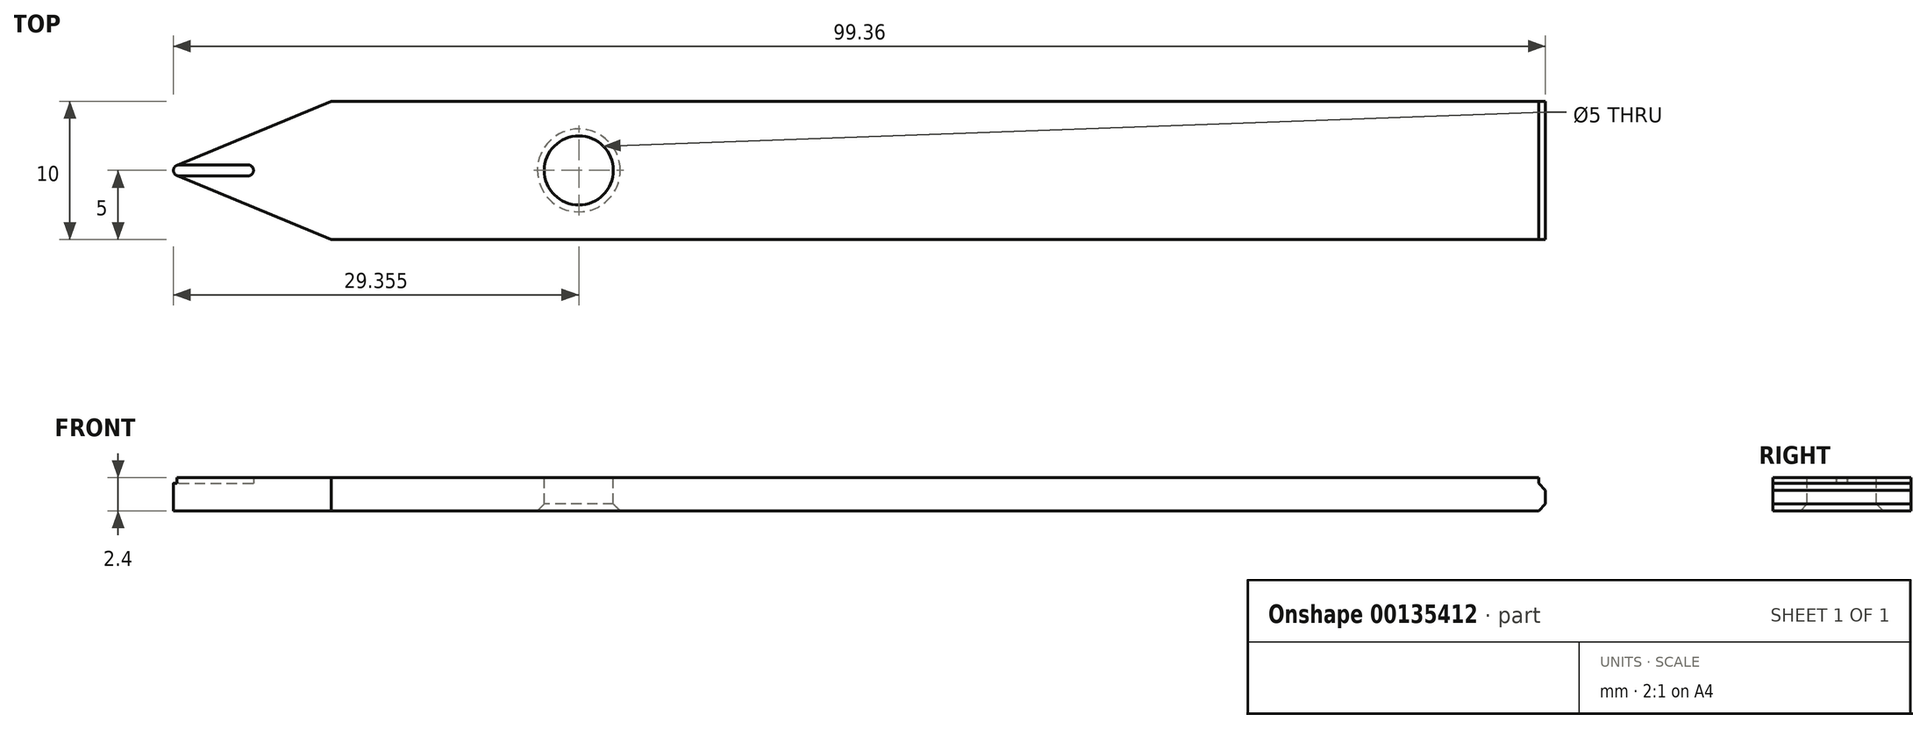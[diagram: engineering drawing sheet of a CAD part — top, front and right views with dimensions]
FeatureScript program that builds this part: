
annotation { "Feature Type Name" : "Feature", "Feature Type Description" : "" }
export const myFeature = defineFeature(function(context is Context, id is Id, definition is map)
    precondition{}
    {
        {
            var Q0;
            Q0=qCreatedBy(makeId("Top.planeOp"),FACE);
            var sketch = newSketch(context, id + "F0", { "sketchPlane" : qUnion([Q0])});
            skLineSegment(sketch, "E0", {"start": v(1.57, 0) * mm, "end": v(-86.36, 0) * mm});
            skLineSegment(sketch, "E1", {"start": v(-86.36, 0) * mm, "end": v(-98.43, -5) * mm});
            skLineSegment(sketch, "E2", {"start": v(-98.43, -5) * mm, "end": v(-86.36, -10) * mm});
            skLineSegment(sketch, "E3", {"start": v(-86.36, -10) * mm, "end": v(1.57, -10) * mm});
            skLineSegment(sketch, "E4", {"start": v(1.57, -10) * mm, "end": v(1.57, 0) * mm});
            skLineSegment(sketch, "E5", {"start": v(-98.43, -5) * mm, "end": v(-67.6, -5) * mm, "construction": true});
            skSolve(sketch);
        }
        {
            var Q0;
            Q0 = qSketchRegion(id + "F0", true);
            extrude(context, id + "F1", {"entities" : qUnion([Q0]), "depth" : 2 * mm});
        }
        {
            var Q0;
            Q0=makeQuery(id+"F1.opExtrude","CAP_FACE",FACE,{"disambiguationData":[OSD([sQuery(id+"F0.wireOp",EDGE,"E0"),sQuery(id+"F0.wireOp",EDGE,"E1"),sQuery(id+"F0.wireOp",EDGE,"E2"),sQuery(id+"F0.wireOp",EDGE,"E3"),sQuery(id+"F0.wireOp",EDGE,"E4")])],"isStart":false});
            var sketch = newSketch(context, id + "F2", { "sketchPlane" : qUnion([Q0])});
            skLineSegment(sketch, "E6", {"start": v(-98.43, -5) * mm, "end": v(-68.43, -5) * mm, "construction": true});
            skCircle(sketch, "E7", {"center": v(-68.43, -5) * mm, "radius": 2.5 * mm});
            skSolve(sketch);
        }
        {
            var Q0;
            Q0 = qSketchRegion(id + "F2", true);
            var Q1;
            Q1=makeQuery(id+"F2.imprint","IMPRINT",FACE,{"disambiguationData":[TD([[makeQuery(id+"F2.imprint","IMPRINT",EDGE,{"derivedFrom":sQuery(id+"F2.wireOp",EDGE,"E7")}),1.0]])]});
            extrude(context, id + "F3", {"entities" : qUnion([Q0, Q1]), "operationType" : NewBodyOperationType.REMOVE, "oppositeDirection" : true, "depth" : 25 * mm});
        }
        {
            var Q0;
            Q0=makeQuery(id+"F3.boolean.opBoolean","COPY",EDGE,{"derivedFrom":makeQuery(id+"F3.opExtrude","CAP_EDGE",EDGE,{"disambiguationData":[OSD([sQuery(id+"F2.wireOp",EDGE,"E7")])],"isStart":true})});
            var Q1;
            Q1=makeQuery(id+"F3.boolean.opBoolean","INTERSECT",EDGE,{"derivedFrom":[makeQuery(id+"F1.opExtrude","CAP_FACE",FACE,{"disambiguationData":[OSD([sQuery(id+"F0.wireOp",EDGE,"E0"),sQuery(id+"F0.wireOp",EDGE,"E1"),sQuery(id+"F0.wireOp",EDGE,"E2"),sQuery(id+"F0.wireOp",EDGE,"E3"),sQuery(id+"F0.wireOp",EDGE,"E4")])],"isStart":true}),makeQuery(id+"F3.opExtrude","SWEPT_FACE",FACE,{"disambiguationData":[OSD([sQuery(id+"F2.wireOp",EDGE,"E7")])]})]});
            chamfer(context, id + "F4", {"entities" : qUnion([Q0, Q1]), "width" : 0.5 * mm, "tangentPropagation" : true});
        }
        {
            var Q0;
            Q0=makeQuery(id+"F1.opExtrude","CAP_EDGE",EDGE,{"disambiguationData":[OSD([sQuery(id+"F0.wireOp",EDGE,"E4")])],"isStart":false});
            var Q1;
            Q1=makeQuery(id+"F1.opExtrude","CAP_EDGE",EDGE,{"disambiguationData":[OSD([sQuery(id+"F0.wireOp",EDGE,"E4")])],"isStart":true});
            chamfer(context, id + "F5", {"entities" : qUnion([Q0, Q1]), "width" : 0.5 * mm, "tangentPropagation" : true});
        }
        {
            var Q0;
            Q0=makeQuery(id+"F1.opExtrude","SWEPT_EDGE",EDGE,{"disambiguationData":[OSD([sQuery(id+"F0.wireOp",EDGE,"E1"),sQuery(id+"F0.wireOp",EDGE,"E2")])]});
            fillet(context, id + "F6", {"entities" : qUnion([Q0]), "radius" : 0.4 * mm, "tangentPropagation" : true, "allowEdgeOverflow" : false});
        }
        {
            var Q0;
            Q0=makeQuery(id+"F1.opExtrude","CAP_FACE",FACE,{"disambiguationData":[OSD([sQuery(id+"F0.wireOp",EDGE,"E0"),sQuery(id+"F0.wireOp",EDGE,"E1"),sQuery(id+"F0.wireOp",EDGE,"E2"),sQuery(id+"F0.wireOp",EDGE,"E3"),sQuery(id+"F0.wireOp",EDGE,"E4")])],"isStart":false});
            var sketch = newSketch(context, id + "F7", { "sketchPlane" : qUnion([Q0])});
            skPoint(sketch, "E8.endSnap0", {"position": v(-97.79, -5) * mm});
            skLineSegment(sketch, "E9", {"start": v(-97.39, -5) * mm, "end": v(-92.39, -5) * mm});
            skArc(sketch, "E10.0.startCap", {"start": v(-97.39, -5.4) * mm, "mid": v(-97.79, -5) * mm, "end": v(-97.39, -4.6) * mm});
            skArc(sketch, "E10.0.endCap", {"start": v(-92.39, -4.6) * mm, "mid": v(-91.99, -5) * mm, "end": v(-92.39, -5.4) * mm});
            skLineSegment(sketch, "E10.0.left", {"start": v(-97.39, -4.6) * mm, "end": v(-92.39, -4.6) * mm});
            skLineSegment(sketch, "E10.0.right", {"start": v(-97.39, -5.4) * mm, "end": v(-92.39, -5.4) * mm});
            skSolve(sketch);
        }
        {
            var Q0;
            Q0=makeQuery(id+"F7.imprint","IMPRINT",FACE,{"disambiguationData":[TD([[makeQuery(id+"F7.imprint","IMPRINT",EDGE,{"derivedFrom":sQuery(id+"F7.wireOp",EDGE,"E10.0.endCap")}),-1.0]])]});
            extrude(context, id + "F8", {"entities" : qUnion([Q0]), "operationType" : NewBodyOperationType.ADD, "depth" : 0.4 * mm});
        }
    });
